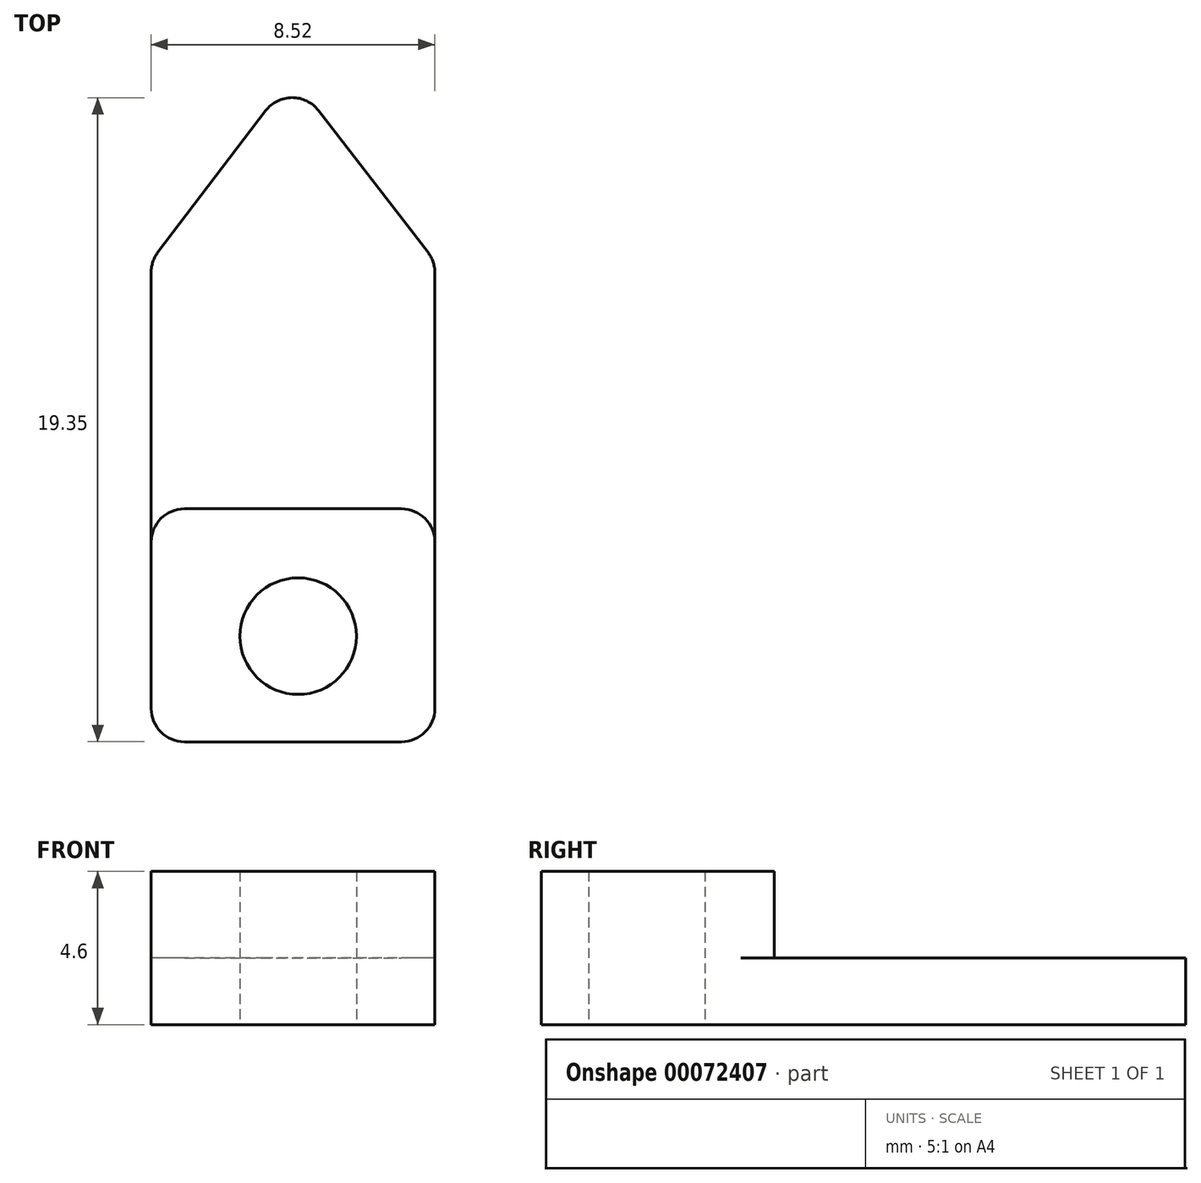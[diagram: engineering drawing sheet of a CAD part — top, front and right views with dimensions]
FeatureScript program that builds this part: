
annotation { "Feature Type Name" : "Feature", "Feature Type Description" : "" }
export const myFeature = defineFeature(function(context is Context, id is Id, definition is map)
    precondition{}
    {
        {
            var Q0;
            Q0=qCreatedBy(makeId("Top.planeOp"),FACE);
            var sketch = newSketch(context, id + "F0", { "sketchPlane" : qUnion([Q0])});
            skLineSegment(sketch, "E0", {"start": v(-17.2, -9.14) * mm, "end": v(-8.69, -9.14) * mm});
            skLineSegment(sketch, "E1", {"start": v(-8.69, -9.14) * mm, "end": v(-8.69, 5.3) * mm});
            skLineSegment(sketch, "E2", {"start": v(-8.69, 5.3) * mm, "end": v(-12.98, 10.86) * mm});
            skLineSegment(sketch, "E3", {"start": v(-12.98, 10.86) * mm, "end": v(-17.2, 5.3) * mm});
            skLineSegment(sketch, "E4", {"start": v(-17.2, -9.14) * mm, "end": v(-17.2, 5.3) * mm});
            skLineSegment(sketch, "E5", {"start": v(-16.24, -2.14) * mm, "end": v(-17.2, -2.14) * mm});
            skLineSegment(sketch, "E6", {"start": v(-17.2, -2.14) * mm, "end": v(-8.69, -2.14) * mm});
            skCircle(sketch, "E7", {"center": v(-12.8, -5.97) * mm, "radius": 1.75 * mm});
            skSolve(sketch);
        }
        {
            var Q0;
            {var subQ4=sQuery(id+"F0.wireOp",EDGE,"E0");Q0=makeQuery(id+"F0.imprint","IMPRINT",FACE,{"disambiguationData":[TD([[makeQuery(id+"F0.imprint","IMPRINT",EDGE,{"derivedFrom":subQ4}),1.0]])]});}
            extrude(context, id + "F1", {"entities" : qUnion([Q0]), "depth" : 4.6 * mm});
        }
        {
            var Q0;
            {var subQ4=sQuery(id+"F0.wireOp",EDGE,"E2");Q0=makeQuery(id+"F0.imprint","IMPRINT",FACE,{"disambiguationData":[TD([[makeQuery(id+"F0.imprint","IMPRINT",EDGE,{"derivedFrom":subQ4}),1.0]])]});}
            extrude(context, id + "F2", {"entities" : qUnion([Q0]), "operationType" : NewBodyOperationType.ADD, "depth" : 2 * mm});
        }
        {
            var Q0;
            Q0=makeQuery(id+"F1.opExtrude","SWEPT_EDGE",EDGE,{"disambiguationData":[OSD([sQuery(id+"F0.wireOp",EDGE,"E0"),sQuery(id+"F0.wireOp",EDGE,"E1")])]});
            fillet(context, id + "F3", {"entities" : qUnion([Q0]), "radius" : 1 * mm, "tangentPropagation" : true, "allowEdgeOverflow" : false});
        }
        {
            var Q0;
            Q0=makeQuery(id+"F1.opExtrude","SWEPT_EDGE",EDGE,{"disambiguationData":[OSD([sQuery(id+"F0.wireOp",EDGE,"E0"),sQuery(id+"F0.wireOp",EDGE,"E4")])]});
            fillet(context, id + "F4", {"entities" : qUnion([Q0]), "radius" : 1 * mm, "tangentPropagation" : true, "allowEdgeOverflow" : false});
        }
        {
            var Q0;
            Q0=makeQuery(id+"F1.opExtrude","SWEPT_EDGE",EDGE,{"disambiguationData":[OSD([sQuery(id+"F0.wireOp",EDGE,"E4"),sQuery(id+"F0.wireOp",EDGE,"E6")])]});
            fillet(context, id + "F5", {"entities" : qUnion([Q0]), "radius" : 1 * mm, "tangentPropagation" : true, "allowEdgeOverflow" : false});
        }
        {
            var Q0;
            Q0=makeQuery(id+"F1.opExtrude","SWEPT_EDGE",EDGE,{"disambiguationData":[OSD([sQuery(id+"F0.wireOp",EDGE,"E1"),sQuery(id+"F0.wireOp",EDGE,"E6")])]});
            var Q1;
            Q1=makeQuery(id+"F2.opExtrude","SWEPT_EDGE",EDGE,{"disambiguationData":[OSD([sQuery(id+"F0.wireOp",EDGE,"E2"),sQuery(id+"F0.wireOp",EDGE,"E3")])]});
            var Q2;
            Q2=makeQuery(id+"F2.opExtrude","SWEPT_EDGE",EDGE,{"disambiguationData":[OSD([sQuery(id+"F0.wireOp",EDGE,"E1"),sQuery(id+"F0.wireOp",EDGE,"E2")])]});
            var Q3;
            Q3=makeQuery(id+"F2.opExtrude","SWEPT_EDGE",EDGE,{"disambiguationData":[OSD([sQuery(id+"F0.wireOp",EDGE,"E3"),sQuery(id+"F0.wireOp",EDGE,"E4")])]});
            fillet(context, id + "F6", {"entities" : qUnion([Q0, Q1, Q2, Q3]), "radius" : 1 * mm, "tangentPropagation" : true, "allowEdgeOverflow" : false});
        }
    });
